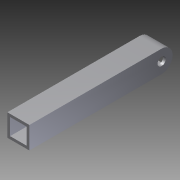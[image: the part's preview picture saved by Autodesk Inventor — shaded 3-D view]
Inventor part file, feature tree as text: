
AUTODESK INVENTOR PART (.ipt)
format: ipt  version: 2012 (Build 160160000, 160)  size: 96,256 bytes
history: native  units: in
note: dims shown in document units (in); Inventor stores cm internally (conversion verified against a paired STEP export)
features: extrude x2, sketch x2
ambient origin geometry x8: Origin, YZ Plane, XZ Plane, XY Plane, X Axis, Y Axis, Z Axis, Center Point
bodies: Solid1 (feature_tree)
feature tree (4):
  extrude  "Extrusion1"  Depth=1.0in
  extrude  "Extrusion2"  Depth=0.125in
  sketch  "Sketch1"  dims[d0=1.0in d1=1.0in]
  sketch  "Sketch2"  dims[d2=0.125in d3=0.125in d4=0.125in d5=0.125in d6=6.5in d7=0.0in d8=0.375in d9=0.5in d10=0.5in d11=1.0in d12=0.0in]
